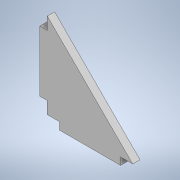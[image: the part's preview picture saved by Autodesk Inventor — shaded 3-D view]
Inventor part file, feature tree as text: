
AUTODESK INVENTOR PART (.ipt)
format: ipt  version: 2020 (Build 240168000, 168)  size: 130,048 bytes
history: native  units: in
note: dims shown in document units (in); Inventor stores cm internally (conversion verified against a paired STEP export)
features: extrude x4, sketch x4
ambient origin geometry x8: Origin, YZ Plane, XZ Plane, XY Plane, X Axis, Y Axis, Z Axis, Center Point
bodies: Solid1 (feature_tree)
feature tree (8):
  extrude  "Extrusion1"  Depth=0.1969in
  extrude  "Extrusion2"  Depth=0.1969in
  extrude  "Extrusion3"  Depth=0.1969in
  extrude  "Extrusion4"  Depth=0.1181in
  sketch  "Sketch1"  dims[d2=0.1969in d3=0.1969in]
  sketch  "Sketch2"  dims[d4=0.3937in d5=0.1969in]
  sketch  "Sketch3"  dims[d6=0.3937in d7=0.1969in]
  sketch  "Sketch4"  dims[d12=0.1181in d13=0.0in d14=0.5906in d15=0.5906in d16=0.1181in d17=0.0in d18=0.5906in d19=0.0in d20=0.5906in d21=0.0in]
